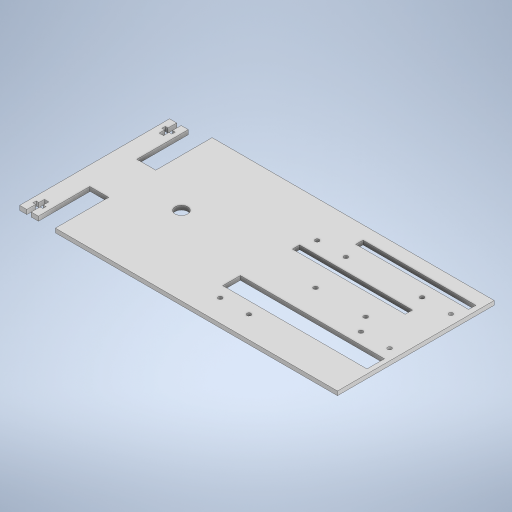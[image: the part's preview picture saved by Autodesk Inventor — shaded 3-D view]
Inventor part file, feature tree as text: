
AUTODESK INVENTOR PART (.ipt)
format: ipt  version: 2024 (Build 280153020, 153B)  size: 439,296 bytes
history: native  units: mm
features: extrude x8, sketch x7
ambient origin geometry x8: Origin, YZ Plane, XZ Plane, XY Plane, X Axis, Y Axis, Z Axis, Center Point
bodies: Solid1 (feature_tree)
feature tree (15):
  sketch  "Sketch1"  dims[d0=195.0mm d1=125.0mm]
  extrude  "Extrusion1"  Depth=125.0mm
  extrude  "Extrusion2"  Depth=40.0mm
  extrude  "Extrusion4"  Depth=41.0mm
  extrude  "Extrusion5"  Depth=3.25mm
  extrude  "Extrusion6"  Depth=1.75mm
  extrude  "Extrusion7"  Depth=30.0mm
  extrude  "Extrusion8"  Depth=1.5mm
  extrude  "Extrusion9"  Depth=3.5mm
  sketch  "Sketch2"  dims[d3=30.0mm d4=40.0mm]
  sketch  "Sketch3"  dims[d5=15.0mm d6=41.0mm]
  sketch  "Sketch4"  dims[d9=3.25mm d10=0.0mm d11=7.5mm]
  sketch  "Sketch5"  dims[d12=1.8mm d13=1.75mm]
  sketch  "Sketch6"  dims[d15=2.0mm d21=30.0mm]
  sketch  "Sketch7"  dims[d22=8.692185mm d23=1.5mm d28=18.0mm d29=30.0mm d30=18.0mm d31=68.0mm d32=10.0mm d33=10.0mm d34=0.0mm d35=20.0mm d36=125.0mm d39=30.0mm d40=0.0mm d41=20.0mm d42=3.2mm d43=20.0mm d45=4.0mm d46=0.0mm d47=3.2mm d48=88.2mm d49=17.6mm d50=3.2mm d51=3.2mm d52=22.88mm d53=50.3mm d54=8.7mm d55=3.2mm d56=3.2mm d57=22.88mm d58=8.0mm d59=26.6mm d60=3.2mm d61=22.88mm d62=3.2mm d63=89.18mm d64=29.1mm d65=3.2mm d66=22.88mm d67=3.2mm d68=10.0mm d69=0.0mm d71=45.0mm d72=90.0mm d73=5.76mm d74=10.0mm d75=0.0mm d76=4.0mm d78=45.0mm d79=90.0mm d80=5.75mm d82=26.0mm d84=45.0mm d85=115.0mm d86=14.0mm d87=3.5mm d88=27.0mm d90=6.0mm d91=3.5mm d92=0.0mm d93=1.75mm d94=1.75mm d95=14.0mm d96=3.5mm d97=2.2mm d98=7.0mm d99=2.6mm d100=3.5mm d101=0.0mm]
